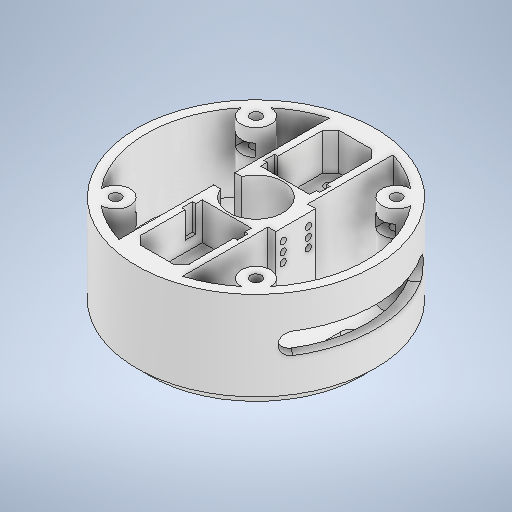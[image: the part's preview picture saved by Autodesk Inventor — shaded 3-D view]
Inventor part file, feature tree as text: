
AUTODESK INVENTOR PART (.ipt)
format: ipt  version: 2025.2 (Build 292293000, 293)  size: 736,768 bytes
history: native  units: mm
features: extrude x15, sketch x12, chamfer x4, plane x1, other x1, fillet x1, mirror x1, projected_geometry x1
ambient origin geometry x8: Origin, YZ Plane, XZ Plane, XY Plane, X Axis, Y Axis, Z Axis, Center Point
bodies: Solid1 (feature_tree)
feature tree (36):
  sketch  "Sketch1"  dims[d0=90.0mm d6=15.0mm d7=0.0mm]
  extrude  "Base"  Depth=15.0mm TaperAngle=0.0deg
  extrude  "M3 nut stop"  Depth=20.5mm
  extrude  "Top"  Depth=31.0mm
  extrude  "Base of shaft support"  Depth=18.5mm
  chamfer  "Corners of shaft support"  Distance=31.0mm
  extrude  "Stepper mount holes"  Depth=8.0mm
  extrude  "Stepper face mount"  Depth=3.0mm TaperAngle=45.0deg
  extrude  "Material reduction"  Depth=6.5mm
  sketch  "Sketch6"  dims[d17=15.0mm]
  extrude  "Slot for M4 fasteners"  Depth=12.0mm
  plane  "Work Plane1"
  extrude  "Slot for M4 nuts to fasen to the swivel base"  Depth=10.0mm
  extrude  "Mounting face for limit switch"  Depth=10.0mm
  extrude  "Mounting holes for limit switch"  TaperAngle=45.0deg  [1 undecoded]
  extrude  "Recess face for stepper mounting"  Depth=10.0mm
  chamfer  "Corner of stepper mounting face"  Distance=4.1mm
  chamfer  "Material reduction at the base"  Distance=30.0mm
  extrude  "Wiring slot 1"  Depth=10.0mm TaperAngle=0.0deg
  other  "Wiring slot 2"
  fillet  "Fillet1"  Radius=3.2mm
  extrude  "Screwing slot"  Depth=10.0mm
  chamfer  "Chamfer4"  Distance=2.4mm
  extrude  "Extrusion15"  Depth=10.0mm TaperAngle=0.0deg
  mirror  "Mirror1"
  sketch  "Sketch4"  dims[d12=20.5mm d13=31.0mm]
  sketch  "Sketch5"  dims[d15=18.5mm d16=15.0mm]
  sketch  "Sketch7"  dims[d18=45.0mm]
  sketch  "Sketch8"  dims[d19=3.0mm d20=31.0mm d21=0.0mm]
  sketch  "Sketch9"  dims[d23=8.0mm d25=3.3mm]
  projected_geometry  "Projected Loop1"
  sketch  "Sketch10"  dims[d27=3.0mm d28=0.0mm d29=3.0mm d30=2.0mm d31=45.0deg]
  sketch  "Sketch11"  dims[d32=6.5mm d33=0.0mm d34=22.0mm]
  sketch  "Sketch Rectangular Pattern1"  dims[d8=20.5mm d9=0.0mm d11=6.0mm]
  sketch  "Sketch12"  dims[d35=2.0mm d36=0.0mm d38=12.0mm]
  sketch  "Sketch13"  dims[d39=34.0mm d40=0.0mm d41=37.5mm d43=11.0mm d44=45.0deg d45=7.5mm d46=4.1mm d47=30.0mm d48=0.0mm d49=-5.0mm d50=4.7mm d51=0.0mm d54=3.2mm d55=0.0mm d56=9.5mm d57=2.4mm d59=3.5mm d60=0.0mm d61=15.0mm d62=3.0mm d63=8.0mm d64=42.5mm d65=3.0mm d66=0.0mm d67=3.5mm d68=2.0mm d69=45.0deg d70=9.0mm d71=26.5mm d72=6.3mm d73=5.0mm d74=2.0mm d75=45.0deg d76=3.5mm d77=12.0mm d78=30.0mm d79=4.0mm d80=34.0mm d81=0.0mm d82=8.0mm d83=8.0mm d84=75.0deg d85=4.0mm d86=3.5mm d87=20.0mm d89=3.5mm d90=10.0mm d92=10.0mm d94=8.0mm d95=20.5mm d96=0.0mm d97=2.0mm d98=2.0mm d99=45.0deg d100=4.0mm d101=21.0mm d102=16.0mm d103=10.0mm d104=0.0mm]
note: 1 required parameter value undecoded (feature->parameter linkage not recoverable at this tier; creation-order binding heuristic only, values carry confidence <= 0.55)
